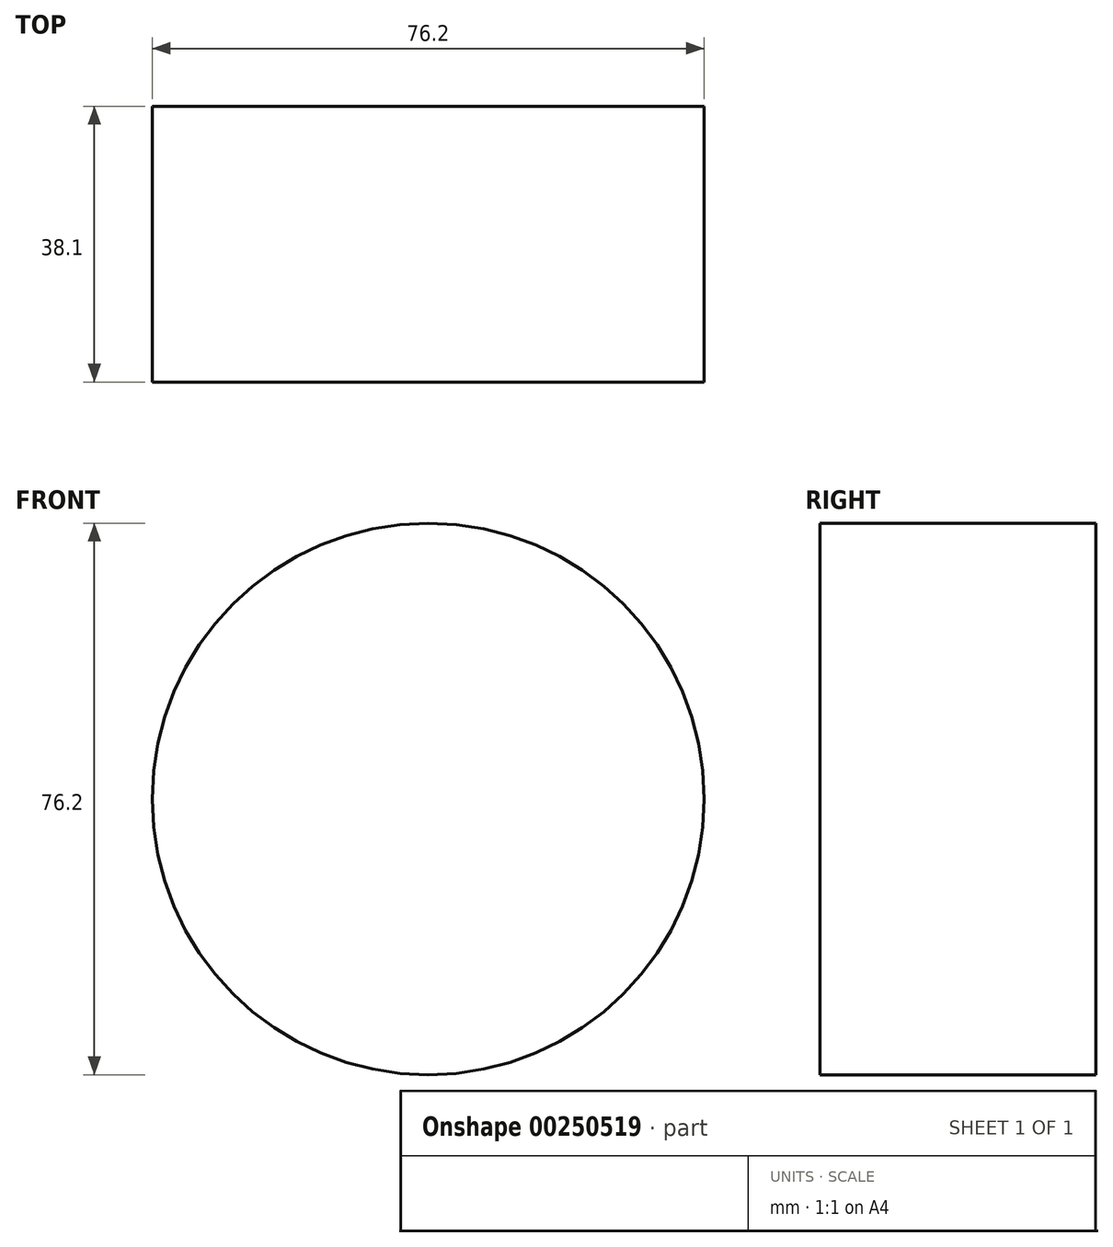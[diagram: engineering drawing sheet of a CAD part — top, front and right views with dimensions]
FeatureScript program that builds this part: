
annotation { "Feature Type Name" : "Feature", "Feature Type Description" : "" }
export const myFeature = defineFeature(function(context is Context, id is Id, definition is map)
    precondition{}
    {
        {
            var Q0;
            Q0=qCreatedBy(makeId("Front.planeOp"),FACE);
            var sketch = newSketch(context, id + "F0", { "sketchPlane" : qUnion([Q0])});
            skCircle(sketch, "E0", {"center": v(0, 0) * mm, "radius": 38.1 * mm});
            skSolve(sketch);
        }
        {
            var Q0;
            Q0=makeQuery(id+"F0.imprint","IMPRINT",FACE,{"disambiguationData":[TD([[makeQuery(id+"F0.imprint","IMPRINT",EDGE,{"derivedFrom":sQuery(id+"F0.wireOp",EDGE,"E0")}),1.0]])]});
            extrude(context, id + "F1", {"entities" : qUnion([Q0]), "endBound" : BoundingType.SYMMETRIC, "oppositeDirection" : true, "depth" : 38.1 * mm});
        }
    });
